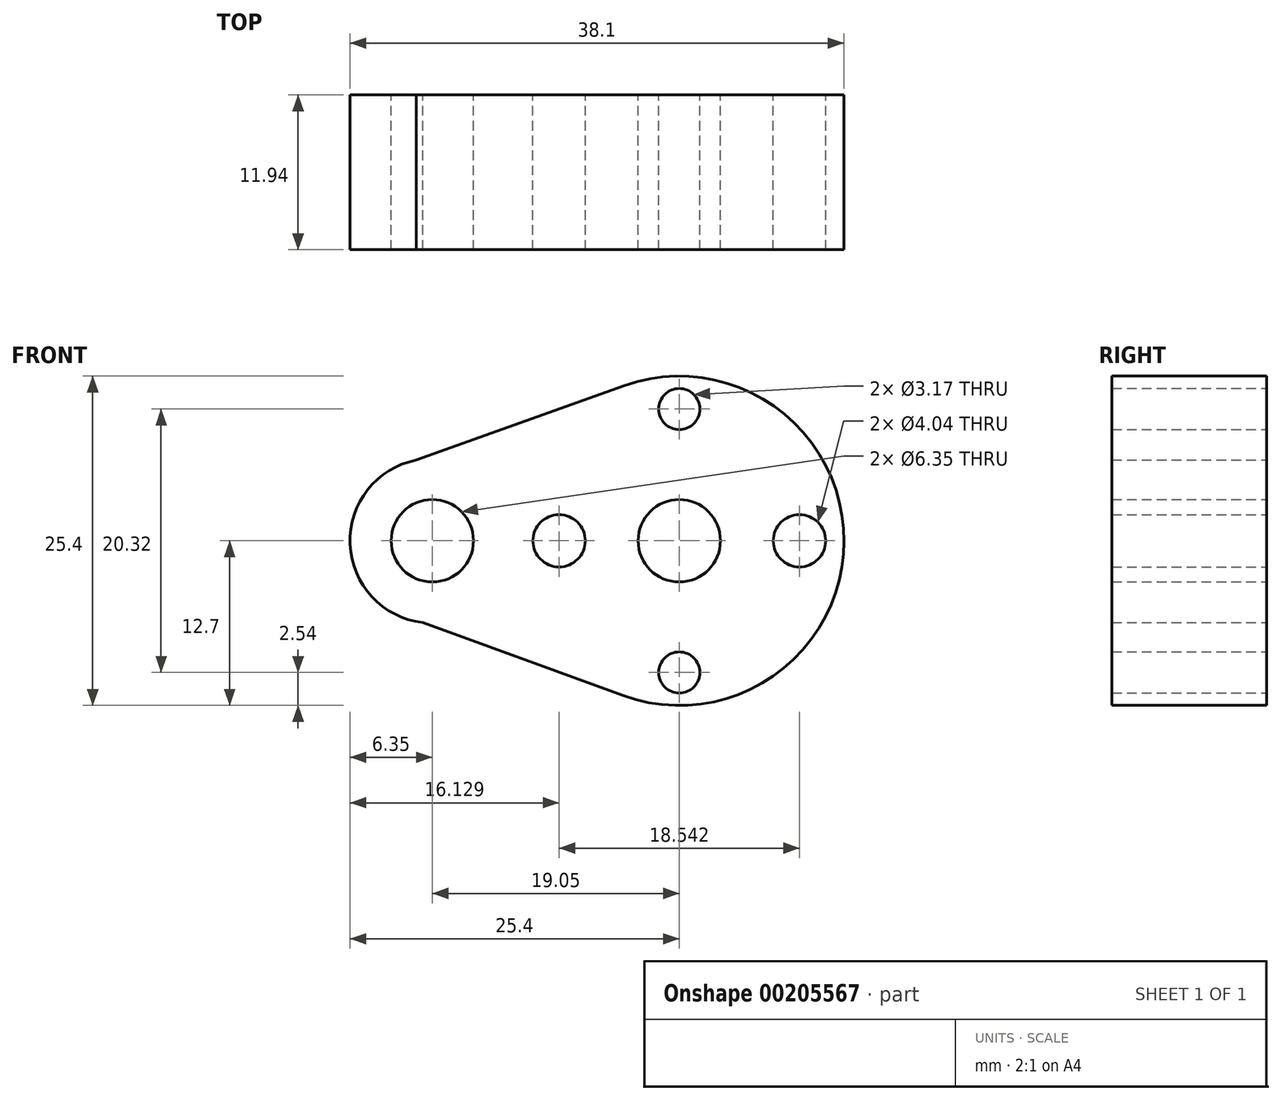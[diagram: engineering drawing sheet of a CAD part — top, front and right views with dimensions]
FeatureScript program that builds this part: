
annotation { "Feature Type Name" : "Feature", "Feature Type Description" : "" }
export const myFeature = defineFeature(function(context is Context, id is Id, definition is map)
    precondition{}
    {
        {
            var Q0;
            Q0=qCreatedBy(makeId("Front.planeOp"),FACE);
            var sketch = newSketch(context, id + "F0", { "sketchPlane" : qUnion([Q0])});
            skCircle(sketch, "E0", {"center": v(0, 0) * mm, "radius": 12.7 * mm});
            skCircle(sketch, "E1", {"center": v(-19.05, 0) * mm, "radius": 6.35 * mm});
            skCircle(sketch, "E2", {"center": v(-19.05, 0) * mm, "radius": 3.18 * mm});
            skCircle(sketch, "E3", {"center": v(0, 0) * mm, "radius": 3.18 * mm});
            skLineSegment(sketch, "E4", {"start": v(-20.28, 6.23) * mm, "end": v(-4.28, 11.96) * mm});
            skLineSegment(sketch, "E5", {"start": v(-19.78, -6.3) * mm, "end": v(-4.35, -11.93) * mm});
            skCircle(sketch, "E6", {"center": v(0, 10.16) * mm, "radius": 1.59 * mm});
            skCircle(sketch, "E7", {"center": v(0, -10.16) * mm, "radius": 1.59 * mm});
            skCircle(sketch, "E8", {"center": v(-9.27, 0) * mm, "radius": 2.02 * mm});
            skCircle(sketch, "E9", {"center": v(9.27, 0) * mm, "radius": 2.02 * mm});
            skSolve(sketch);
        }
        {
            var Q0;
            Q0=qSketchRegion(id+"F0",true);
            extrude(context, id + "F1", {"entities" : qUnion([Q0]), "flatOperationType" : FlatOperationType.REMOVE, "offsetDistance" : 25.4 * mm, "depth" : 11.94 * mm, "domain" : OperationDomain.MODEL});
        }
    });
